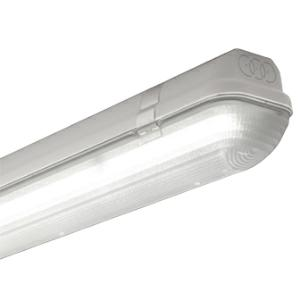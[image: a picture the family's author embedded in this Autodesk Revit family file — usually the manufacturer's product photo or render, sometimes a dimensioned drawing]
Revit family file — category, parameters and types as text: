
# Revit family: 3f_filippi_-_3f_linda_3f_filippi_-_58563_-_3f_linda_led_1x6w_l660
name_source: partatom
category: Lighting Fixtures
units: mm (PartAtom-declared; Revit-internal decimal feet)

## family parameters
Cut with Voids When Loaded = No
Host = Face
Light Source = No
Part Type = Normal
Room Calculation Point = No
Round Connector Dimension = Use Diameter
Shared = No

## types (1)
- 3F Filippi - 3F Linda (1 x LED, 1029 lm, 7.5 W, 4000 K)
    Apparent Load = 8 VA
    Approval mark = CE
    CIE Flux Codes = 44 77 94 97 100
    Color Rendering = 80
    Color Temperature = 4000 K
    Control Gear = Electronic ballast
    Default Elevation = 1800 mm
    Description = ILLUMINOTECHNICAL
Luminous efficiency 100% (DLOR 97%, ULOR 3%).
Initial luminous flux of the luminaire 1029 lm.
Controlled direct symmetric distribution.
Installation Interdistance Transv.D = 1.77 x hu - Long.D = 1.17 x hu.
Tabular UGR (CIE 117 - 4H-8H; S=0.25H; 70/50/20): RUG 19.4 - 20.2.
Beam angle: 109° - 64°.
Luminous efficacy 137 lm/W.
Lifetime (L93/B10): 30000 h. (tq+25°C)
Lifetime (L90/B10): 50000 h. (tq+25°C)
Lifetime (L85/B10): 80000 h. (tq+25°C)
Lifetime (L80/B10): 100000 h. (tq+25°C)
Lifetime (L85/B10): 50000 h. (tq+50°C)
Sudden decreased luminous flux after 50000 hours: 0% (C0).
Photobiological safety in compliance with IEC/TR 62778: RG0 risk exempt, (IEC 62471).
In compliance with IEC/EN 62722-2-1 - IEC/EN 62717 standards.

SOURCE
Linear LED module 6W/840.
Energy efficiency class (UE 2019/2020 - UE 2019/2015): D.
CIE 13.3 Colour rendering index: CRI >80 (R9 <50%).
IES TM-30 Fidelity Index: Rf = 84 Rg = 95.
CCT nominal colour temperature 4000 K.
Colour initial tolerance (MacAdam): SDCM 3.

MECHANICAL
Self-extinguishing V2 polycarbonate housing, injection moulded, RAL 7035 grey.
Ecologic anti-aging injected sealing gasket.
Diffuser in self-extinguishing V2 polycarbonate, photo-engraved interior, UV stabilised, injection moulded with smooth outer surface, tamper-proof opening.
Gear-holder reflector in hot-dip galvanised steel, painted with white polyester base.
Snug fit safety snap-lock clips for diffuser mounting in stainless steel, screwdriver opening.
Fixing brackets in stainless steel.
Possibility for technicians to access the interior of the luminaire.
Luminaire with limited surface temperature. - D - (EN 60598-2-24)
Dimensions: 660x100 mm, height 100 mm. Weight 1.115 kg.
IP66 protection degree.
Mechanical strength to impacts IK10 (20 joule).
Glow-wire test resistance 850°C.

ELECTRICAL
Halogen Free electronic wiring 230V-50/60Hz, power factor 0.90, THD <25%, constant output current, SELV, class I, 1 driver.
Power of the luminaire 7.5 W.
ENEC - CE.
SAFE FLICKER: PstLM=<1 and SVM=<0.4 (IEC TR 61547-1 and IEC TR 63158), to ensure a more comfortable and safe light.
Luminaire compliant with EN 60598-2-22 for power supply from a centralised emergency system CPSS (Central Power Supply System), not incorporated in the luminaire - high risk areas excluded. The default power and flux are 100% in AC and 100% in DC.
Ambient temperature from -20°C to +50°C.
Temperature class T6 max 85°C.
Relative humidity UR: <85%.

INSTALLATION
Ceiling / Suspended / Wall.
All accessories dedicated to this product are available on the Catalog and on our website www.3F-Filippi.com.

APPLICATIONS
Suitable product for food production plants (HACCP), IFS (Food Version 6), BRC (GSFS Food Version 7).
Dry, dusty indoor environments, subject to occasional water splashes.
Virtually shatterproof polycarbonate compatibly with the fumes / atmospheres that compromise the elasticity of plastic materials.
Not suitable for installation on surfaces subject to important vibrations, exposed to weather conditions, on ropes or poles.
Suitable for illumination of public car parks and parking grounds referred to DIN 67528:2018-04.

WARNING
Fixture not suitable for cold stores with an ambient temperature <0°C and/or relative humidity >85%.
Luminaire designed for disposal/recycling at end-of-life.
Replaceable (LED only) light source by a professional. Replaceable control gear by a professional.
    Height = 100 mm  [stored 0.328084 ft]
    Lamp = 1 x LED
    Lamp Light Flux = 1029 lm
    Lamp Power = 7.5 W
    Lamp count = 1
    Length = 660 mm
    Lifetime = 50000 h
    Luminous efficacy = 137 lm/W
    Manufacturer = 3F Filippi
    ModVariant = No
    Model = 3F Filippi - 58563 - 3F Linda LED 1x6W L660
    Mounting Place = Ceiling
    Mounting Type = Pendant
    Number of Poles = 1
    OnlyDefault = Yes
    Power Factor = 1
    Product Name = 3F Filippi - 3F Linda
    Product group = pendant luminaire
    ProductGroupID = 9
    Protection Class = Protection class I
    Protection Degree = IP 66
    RLX_Detail_Level = 1
    RLX_Emergency_Light_Flux = 0 lm
    RLX_Emergency_Type = 0
    RLX_Emergency_Type_DB = No
    RlxData = <blob elided: 69769 chars, md5=7291c69d>
    Socket = socket
    Standby Power = 0 W
    System Light Flux = 1029 lm
    System Power = 8 W
    Type Comments = Product without accessories
    Type Image = 3ffilippi_58563.jpg
    URL = http://relux.com
    VarID = ---
    Voltage = 0 V
    Weight = 0.00 kg
    Width = 100 mm  [stored 0.328084 ft]

note: [stored X ft] marks values corroborated as IEEE doubles in the binary element streams (Revit-internal decimal feet)

## geometry (parser evidence)
native form markers: Blend x4, Sweep x10
no freeform markers — native parametric forms only
